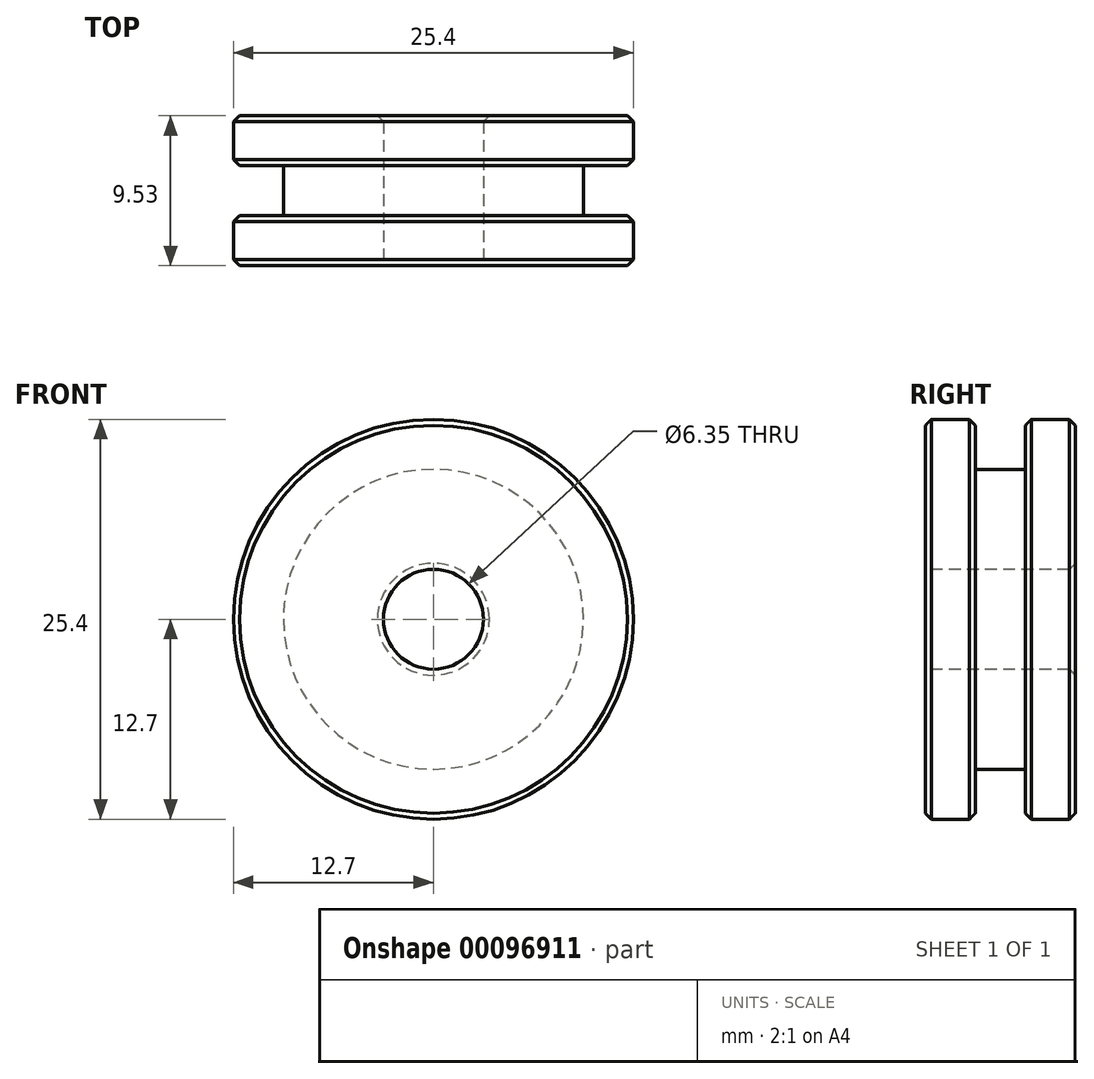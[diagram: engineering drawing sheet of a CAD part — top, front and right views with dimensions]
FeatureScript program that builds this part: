
annotation { "Feature Type Name" : "Feature", "Feature Type Description" : "" }
export const myFeature = defineFeature(function(context is Context, id is Id, definition is map)
    precondition{}
    {
        {
            var Q0;
            Q0=qCreatedBy(makeId("Top.planeOp"),FACE);
            var sketch = newSketch(context, id + "F0", { "sketchPlane" : qUnion([Q0])});
            skLineSegment(sketch, "E0", {"start": v(0, 0) * mm, "end": v(0, 9.52) * mm});
            skLineSegment(sketch, "E1", {"start": v(0, 9.53) * mm, "end": v(12.7, 9.53) * mm});
            skLineSegment(sketch, "E2", {"start": v(12.7, 9.52) * mm, "end": v(12.7, 6.35) * mm});
            skLineSegment(sketch, "E3", {"start": v(12.7, 6.35) * mm, "end": v(9.53, 6.35) * mm});
            skLineSegment(sketch, "E4", {"start": v(9.53, 6.35) * mm, "end": v(9.53, 3.17) * mm});
            skLineSegment(sketch, "E5", {"start": v(9.53, 3.17) * mm, "end": v(12.7, 3.17) * mm});
            skLineSegment(sketch, "E6", {"start": v(12.7, 3.17) * mm, "end": v(12.7, 0) * mm});
            skLineSegment(sketch, "E7", {"start": v(12.7, 0) * mm, "end": v(0, 0) * mm});
            skSolve(sketch);
        }
        {
            var Q0;
            Q0=makeQuery(id+"F0.imprint","IMPRINT",FACE,{"disambiguationData":[TD([[makeQuery(id+"F0.imprint","IMPRINT",EDGE,{"derivedFrom":sQuery(id+"F0.wireOp",EDGE,"E0")}),-1.0]])]});
            var Q1;
            Q1=sQuery(id+"F0.wireOp",EDGE,"E0");
            revolve(context, id + "F1", {"entities" : qUnion([Q0]), "axis" : qUnion([Q1]), "revolveType" : RevolveType.FULL});
        }
        {
            var Q0;
            Q0=makeQuery(id+"F1.opRevolve","SWEPT_FACE",FACE,{"disambiguationData":[OSD([sQuery(id+"F0.wireOp",EDGE,"E7")])]});
            var sketch = newSketch(context, id + "F2", { "sketchPlane" : qUnion([Q0])});
            skCircle(sketch, "E8", {"center": v(0, 0) * mm, "radius": 3.18 * mm});
            skSolve(sketch);
        }
        {
            var Q0;
            Q0 = qSketchRegion(id + "F2", true);
            extrude(context, id + "F3", {"entities" : qUnion([Q0]), "operationType" : NewBodyOperationType.REMOVE, "endBound" : BoundingType.THROUGH_ALL, "oppositeDirection" : true, "depth" : 25.4 * mm});
        }
        {
            var Q0;
            Q0=makeQuery(id+"F3.boolean.opBoolean","COPY",EDGE,{"derivedFrom":makeQuery(id+"F3.opExtrude","CAP_EDGE",EDGE,{"disambiguationData":[OSD([sQuery(id+"F2.wireOp",EDGE,"E8")])],"isStart":true})});
            var Q1;
            Q1=makeQuery(id+"F3.boolean.opBoolean","INTERSECT",EDGE,{"derivedFrom":[makeQuery(id+"F1.opRevolve","SWEPT_FACE",FACE,{"disambiguationData":[OSD([sQuery(id+"F0.wireOp",EDGE,"E1")])]}),makeQuery(id+"F3.opExtrude","SWEPT_FACE",FACE,{"disambiguationData":[OSD([sQuery(id+"F2.wireOp",EDGE,"E8")])]})]});
            var Q2;
            Q2=makeQuery(id+"F1.opRevolve","SWEPT_EDGE",EDGE,{"disambiguationData":[OSD([sQuery(id+"F0.wireOp",EDGE,"E6"),sQuery(id+"F0.wireOp",EDGE,"E7")])]});
            var Q3;
            Q3=makeQuery(id+"F1.opRevolve","SWEPT_EDGE",EDGE,{"disambiguationData":[OSD([sQuery(id+"F0.wireOp",EDGE,"E5"),sQuery(id+"F0.wireOp",EDGE,"E6")])]});
            var Q4;
            Q4=makeQuery(id+"F1.opRevolve","SWEPT_EDGE",EDGE,{"disambiguationData":[OSD([sQuery(id+"F0.wireOp",EDGE,"E2"),sQuery(id+"F0.wireOp",EDGE,"E3")])]});
            var Q5;
            Q5=makeQuery(id+"F1.opRevolve","SWEPT_EDGE",EDGE,{"disambiguationData":[OSD([sQuery(id+"F0.wireOp",EDGE,"E1"),sQuery(id+"F0.wireOp",EDGE,"E2")])]});
            chamfer(context, id + "F4", {"entities" : qUnion([Q0, Q1, Q2, Q3, Q4, Q5]), "width" : 0.38 * mm, "tangentPropagation" : true});
        }
    });
